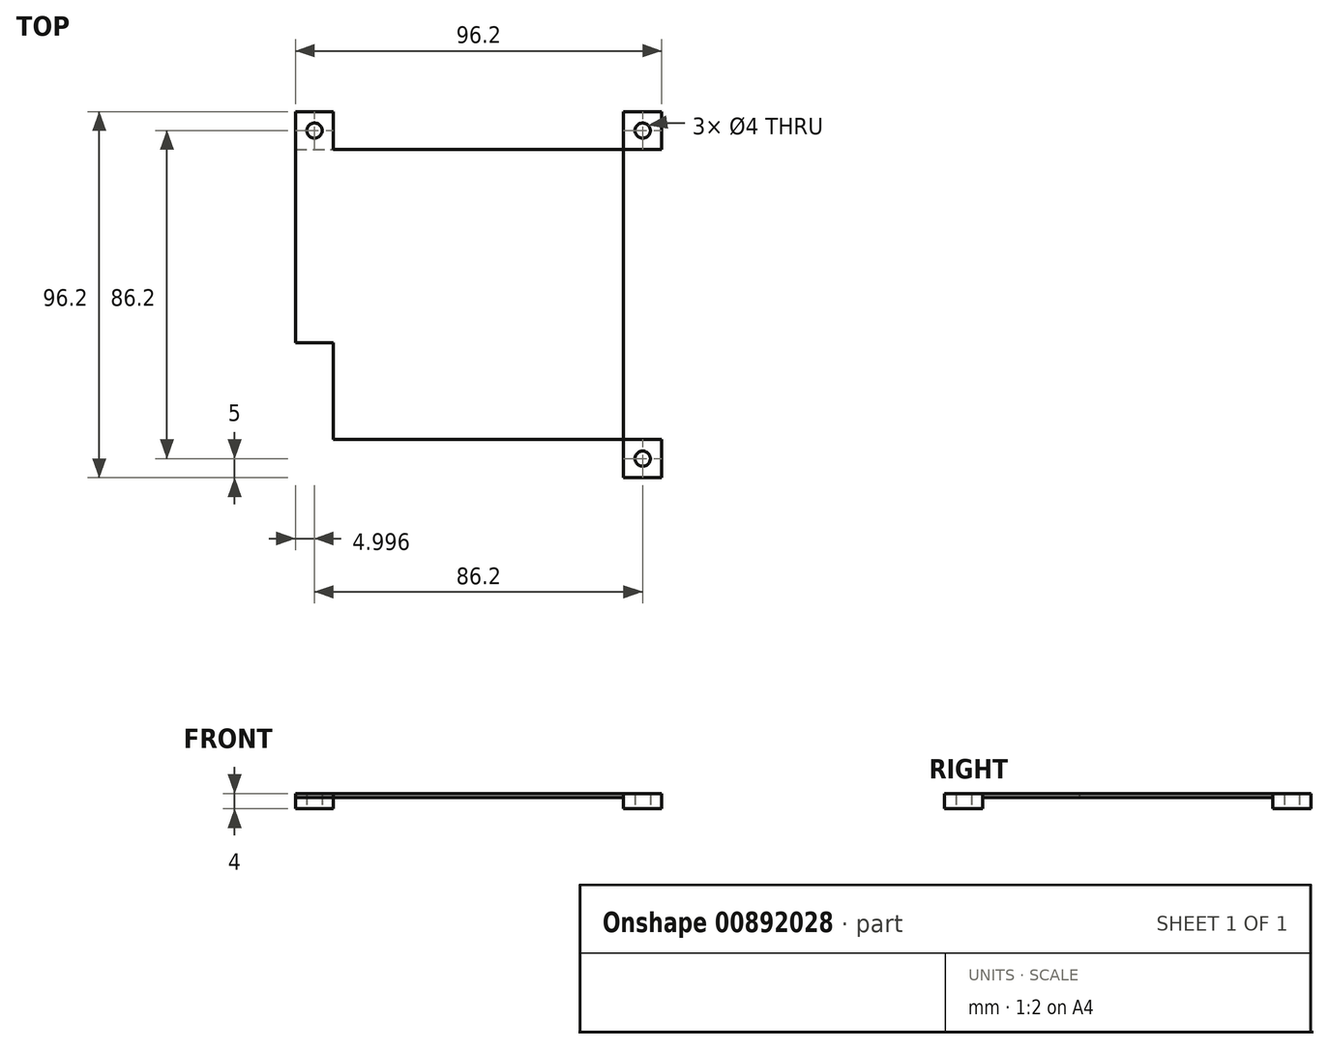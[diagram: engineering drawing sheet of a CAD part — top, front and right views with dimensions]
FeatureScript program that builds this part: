
annotation { "Feature Type Name" : "Feature", "Feature Type Description" : "" }
export const myFeature = defineFeature(function(context is Context, id is Id, definition is map)
    precondition{}
    {
        {
            var Q0;
            Q0=qCreatedBy(makeId("Top.planeOp"),FACE);
            var sketch = newSketch(context, id + "F0", { "sketchPlane" : qUnion([Q0])});
            skLineSegment(sketch, "E0.bottom", {"start": v(-52.37, -47.83) * mm, "end": v(43.83, -47.83) * mm});
            skLineSegment(sketch, "E0.top", {"start": v(-52.37, 48.37) * mm, "end": v(43.83, 48.37) * mm});
            skLineSegment(sketch, "E0.left", {"start": v(-52.37, -47.83) * mm, "end": v(-52.37, 48.37) * mm});
            skLineSegment(sketch, "E0.right", {"start": v(43.83, -47.83) * mm, "end": v(43.83, 48.37) * mm});
            skLineSegment(sketch, "E1.bottom", {"start": v(-52.37, -47.83) * mm, "end": v(-42.37, -47.83) * mm});
            skLineSegment(sketch, "E1.top", {"start": v(-52.37, -37.83) * mm, "end": v(-42.37, -37.83) * mm});
            skLineSegment(sketch, "E1.left", {"start": v(-52.37, -47.83) * mm, "end": v(-52.37, -37.83) * mm});
            skLineSegment(sketch, "E1.right", {"start": v(-42.37, -47.83) * mm, "end": v(-42.37, -37.83) * mm});
            skLineSegment(sketch, "E2.bottom", {"start": v(-42.37, -37.83) * mm, "end": v(33.83, -37.83) * mm});
            skLineSegment(sketch, "E2.top", {"start": v(-42.37, 38.37) * mm, "end": v(33.83, 38.37) * mm});
            skLineSegment(sketch, "E2.left", {"start": v(-42.37, -37.83) * mm, "end": v(-42.37, 38.37) * mm});
            skLineSegment(sketch, "E2.right", {"start": v(33.83, -37.83) * mm, "end": v(33.83, 38.37) * mm});
            skLineSegment(sketch, "E3.bottom", {"start": v(43.83, -47.83) * mm, "end": v(33.83, -47.83) * mm});
            skLineSegment(sketch, "E3.top", {"start": v(43.83, -37.83) * mm, "end": v(33.83, -37.83) * mm});
            skLineSegment(sketch, "E3.left", {"start": v(43.83, -47.83) * mm, "end": v(43.83, -37.83) * mm});
            skLineSegment(sketch, "E3.right", {"start": v(33.83, -47.83) * mm, "end": v(33.83, -37.83) * mm});
            skLineSegment(sketch, "E4.bottom", {"start": v(43.83, 48.37) * mm, "end": v(33.83, 48.37) * mm});
            skLineSegment(sketch, "E4.top", {"start": v(43.83, 38.37) * mm, "end": v(33.83, 38.37) * mm});
            skLineSegment(sketch, "E4.left", {"start": v(43.83, 48.37) * mm, "end": v(43.83, 38.37) * mm});
            skLineSegment(sketch, "E4.right", {"start": v(33.83, 48.37) * mm, "end": v(33.83, 38.37) * mm});
            skLineSegment(sketch, "E5.bottom", {"start": v(-52.37, 48.37) * mm, "end": v(-42.37, 48.37) * mm});
            skLineSegment(sketch, "E5.top", {"start": v(-52.37, 38.37) * mm, "end": v(-42.37, 38.37) * mm});
            skLineSegment(sketch, "E5.left", {"start": v(-52.37, 48.37) * mm, "end": v(-52.37, 38.37) * mm});
            skLineSegment(sketch, "E5.right", {"start": v(-42.37, 48.37) * mm, "end": v(-42.37, 38.37) * mm});
            skLineSegment(sketch, "E6.bottom", {"start": v(-52.37, 38.37) * mm, "end": v(-47.37, 38.37) * mm});
            skLineSegment(sketch, "E6.left", {"start": v(-52.37, 38.37) * mm, "end": v(-52.37, 43.37) * mm});
            skLineSegment(sketch, "E7.bottom", {"start": v(43.83, 38.37) * mm, "end": v(38.83, 38.37) * mm});
            skLineSegment(sketch, "E7.left", {"start": v(43.83, 38.37) * mm, "end": v(43.83, 43.37) * mm});
            skLineSegment(sketch, "E8.bottom", {"start": v(-52.37, -47.83) * mm, "end": v(-47.37, -47.83) * mm});
            skLineSegment(sketch, "E8.left", {"start": v(-52.37, -47.83) * mm, "end": v(-52.37, -42.83) * mm});
            skLineSegment(sketch, "E9.bottom", {"start": v(43.83, -47.83) * mm, "end": v(38.83, -47.83) * mm});
            skLineSegment(sketch, "E9.left", {"start": v(43.83, -47.83) * mm, "end": v(43.83, -42.83) * mm});
            skCircle(sketch, "E10", {"center": v(-47.37, 43.37) * mm, "radius": 2 * mm});
            skCircle(sketch, "E11", {"center": v(38.83, 43.37) * mm, "radius": 2 * mm});
            skCircle(sketch, "E12", {"center": v(-47.37, -42.83) * mm, "radius": 2 * mm});
            skCircle(sketch, "E13", {"center": v(38.83, -42.83) * mm, "radius": 2 * mm});
            skLineSegment(sketch, "E14.left", {"start": v(-42.37, -37.83) * mm, "end": v(-42.37, -37.58) * mm});
            skLineSegment(sketch, "E14.right", {"start": v(33.83, -37.83) * mm, "end": v(33.83, -37.58) * mm});
            skLineSegment(sketch, "E15.bottom", {"start": v(-42.37, 38.37) * mm, "end": v(-42.12, 38.37) * mm});
            skLineSegment(sketch, "E15.top", {"start": v(-42.37, -37.83) * mm, "end": v(-42.12, -37.83) * mm});
            skLineSegment(sketch, "E16.left", {"start": v(-42.37, 38.37) * mm, "end": v(-42.37, 38.12) * mm});
            skLineSegment(sketch, "E16.right", {"start": v(33.83, 38.37) * mm, "end": v(33.83, 38.12) * mm});
            skLineSegment(sketch, "E17.bottom", {"start": v(33.83, 38.37) * mm, "end": v(33.57, 38.37) * mm});
            skLineSegment(sketch, "E17.top", {"start": v(33.83, -37.83) * mm, "end": v(33.57, -37.83) * mm});
            skLineSegment(sketch, "E17.left", {"start": v(33.83, 38.37) * mm, "end": v(33.83, -37.83) * mm});
            skLineSegment(sketch, "E18.bottom", {"start": v(-42.37, -37.83) * mm, "end": v(-38.44, -37.83) * mm});
            skLineSegment(sketch, "E19.left", {"start": v(-42.37, -37.83) * mm, "end": v(-42.37, -36.08) * mm});
            skLineSegment(sketch, "E20.left", {"start": v(-42.37, -37.83) * mm, "end": v(-42.37, -33.9) * mm});
            skLineSegment(sketch, "E21.left", {"start": v(33.83, -37.83) * mm, "end": v(33.83, -33.9) * mm});
            skLineSegment(sketch, "E22.bottom", {"start": v(33.95, -37.83) * mm, "end": v(33.83, -37.83) * mm});
            skLineSegment(sketch, "E23.bottom", {"start": v(33.83, -37.83) * mm, "end": v(29.89, -37.83) * mm});
            skLineSegment(sketch, "E24.left", {"start": v(-42.37, 38.37) * mm, "end": v(-42.37, 34.43) * mm});
            skLineSegment(sketch, "E25.bottom", {"start": v(-42.37, 38.37) * mm, "end": v(-38.44, 38.37) * mm});
            skLineSegment(sketch, "E26.bottom", {"start": v(34.07, 38.37) * mm, "end": v(33.83, 38.37) * mm});
            skLineSegment(sketch, "E26.left", {"start": v(33.83, 38.5) * mm, "end": v(33.83, 38.37) * mm});
            skLineSegment(sketch, "E26.right", {"start": v(34.07, 38.5) * mm, "end": v(34.07, 38.37) * mm});
            skLineSegment(sketch, "E27.left", {"start": v(33.83, 38.37) * mm, "end": v(33.83, 34.43) * mm});
            skLineSegment(sketch, "E28.top", {"start": v(33.83, 38.37) * mm, "end": v(29.89, 38.37) * mm});
            skLineSegment(sketch, "E28.left", {"start": v(33.83, 38.12) * mm, "end": v(33.83, 38.37) * mm});
            skLineSegment(sketch, "E29.bottom", {"start": v(33.83, -37.83) * mm, "end": v(5.89, -37.83) * mm});
            skLineSegment(sketch, "E29.left", {"start": v(33.83, -37.83) * mm, "end": v(33.83, 16.78) * mm});
            skLineSegment(sketch, "E30.bottom", {"start": v(33.83, -37.83) * mm, "end": v(2.25, -37.83) * mm});
            skLineSegment(sketch, "E30.left", {"start": v(33.83, -37.83) * mm, "end": v(33.83, -1.63) * mm});
            skLineSegment(sketch, "E31.bottom", {"start": v(33.83, -37.83) * mm, "end": v(13.3, -37.83) * mm});
            skLineSegment(sketch, "E31.left", {"start": v(33.83, -37.83) * mm, "end": v(33.83, -19.92) * mm});
            skLineSegment(sketch, "E32.bottom", {"start": v(33.83, -37.83) * mm, "end": v(30.27, -37.83) * mm});
            skLineSegment(sketch, "E32.left", {"start": v(33.83, -37.83) * mm, "end": v(33.83, 22.77) * mm});
            skLineSegment(sketch, "E33.bottom", {"start": v(33.83, -37.83) * mm, "end": v(31.29, -37.83) * mm});
            skLineSegment(sketch, "E33.left", {"start": v(33.83, -37.83) * mm, "end": v(33.83, -6.08) * mm});
            skLineSegment(sketch, "E34.bottom", {"start": v(33.83, -37.83) * mm, "end": v(33.32, -37.83) * mm});
            skLineSegment(sketch, "E34.left", {"start": v(33.83, -37.83) * mm, "end": v(33.83, -20.05) * mm});
            skLineSegment(sketch, "E35.top", {"start": v(-52.37, -12.43) * mm, "end": v(-42.37, -12.43) * mm});
            skLineSegment(sketch, "E35.left", {"start": v(-52.37, 38.37) * mm, "end": v(-52.37, -12.43) * mm});
            skLineSegment(sketch, "E35.right", {"start": v(-42.37, 38.37) * mm, "end": v(-42.37, -12.43) * mm});
            skSolve(sketch);
        }
        {
            var Q0;
            Q0=makeQuery(id+"F0.imprint","IMPRINT",FACE,{"disambiguationData":[TD([[makeQuery(id+"F0.imprint","IMPRINT",EDGE,{"derivedFrom":sQuery(id+"F0.wireOp",EDGE,"E4.bottom")}),1.0]])]});
            var Q1;
            Q1=makeQuery(id+"F0.imprint","IMPRINT",FACE,{"disambiguationData":[TD([[makeQuery(id+"F0.imprint","IMPRINT",EDGE,{"derivedFrom":sQuery(id+"F0.wireOp",EDGE,"E0.top")}),-1.0]])]});
            var Q2;
            Q2=makeQuery(id+"F0.imprint","IMPRINT",FACE,{"disambiguationData":[TD([[makeQuery(id+"F0.imprint","IMPRINT",EDGE,{"derivedFrom":sQuery(id+"F0.wireOp",EDGE,"E0.right")}),1.0]])]});
            var Q3;
            Q3=makeQuery(id+"F0.imprint","IMPRINT",FACE,{"disambiguationData":[TD([[makeQuery(id+"F0.imprint","IMPRINT",EDGE,{"derivedFrom":sQuery(id+"F0.wireOp",EDGE,"E5.bottom")}),-1.0]])]});
            var Q4;
            {var subQ1=sQuery(id+"F0.wireOp",EDGE,"E35.top");Q4=makeQuery(id+"F0.imprint","IMPRINT",FACE,{"disambiguationData":[TD([[makeQuery(id+"F0.imprint","IMPRINT",EDGE,{"derivedFrom":subQ1}),1.0]])]});}
            var Q5;
            Q5=makeQuery(id+"F0.imprint","IMPRINT",FACE,{"disambiguationData":[TD([[makeQuery(id+"F0.imprint","IMPRINT",EDGE,{"derivedFrom":sQuery(id+"F0.wireOp",EDGE,"E1.bottom")}),1.0]])]});
            var Q6;
            Q6=makeQuery(id+"F0.imprint","IMPRINT",FACE,{"disambiguationData":[TD([[makeQuery(id+"F0.imprint","IMPRINT",EDGE,{"derivedFrom":sQuery(id+"F0.wireOp",EDGE,"E0.bottom")}),1.0]])]});
            var Q7;
            Q7=makeQuery(id+"F0.imprint","IMPRINT",FACE,{"disambiguationData":[TD([[makeQuery(id+"F0.imprint","IMPRINT",EDGE,{"derivedFrom":sQuery(id+"F0.wireOp",EDGE,"E3.bottom")}),-1.0]])]});
            extrude(context, id + "F1", {"entities" : qUnion([Q0, Q1, Q2, Q3, Q4, Q5, Q6, Q7]), "depth" : 4 * mm, "offsetDistance" : 25 * mm});
        }
        {
            var Q0;
            Q0=makeQuery(id+"F0.imprint","IMPRINT",FACE,{"disambiguationData":[TD([[makeQuery(id+"F0.imprint","IMPRINT",EDGE,{"derivedFrom":sQuery(id+"F0.wireOp",EDGE,"E0.left")}),-1.0]])]});
            var Q1;
            {var subQ19=sQuery(id+"F0.wireOp",EDGE,"E2.left");Q1=makeQuery(id+"F0.imprint","IMPRINT",FACE,{"disambiguationData":[TD([[makeQuery(id+"F0.imprint","IMPRINT",EDGE,{"derivedFrom":subQ19}),-1.0]])]});}
            extrude(context, id + "F2", {"entities" : qUnion([Q0, Q1]), "operationType" : NewBodyOperationType.ADD, "depth" : 4 * mm, "offsetDistance" : 25 * mm});
        }
        {
            var Q0;
            {var subQ19=sQuery(id+"F0.wireOp",EDGE,"E2.left");Q0=makeQuery(id+"F0.imprint","IMPRINT",FACE,{"disambiguationData":[TD([[makeQuery(id+"F0.imprint","IMPRINT",EDGE,{"derivedFrom":subQ19}),-1.0]])]});}
            var Q1;
            {var subQ1=sQuery(id+"F0.wireOp",EDGE,"E35.top");Q1=makeQuery(id+"F0.imprint","IMPRINT",FACE,{"disambiguationData":[TD([[makeQuery(id+"F0.imprint","IMPRINT",EDGE,{"derivedFrom":subQ1}),1.0]])]});}
            extrude(context, id + "F3", {"entities" : qUnion([Q0, Q1]), "operationType" : NewBodyOperationType.REMOVE, "depth" : 3 * mm, "offsetDistance" : 25 * mm});
        }
    });
